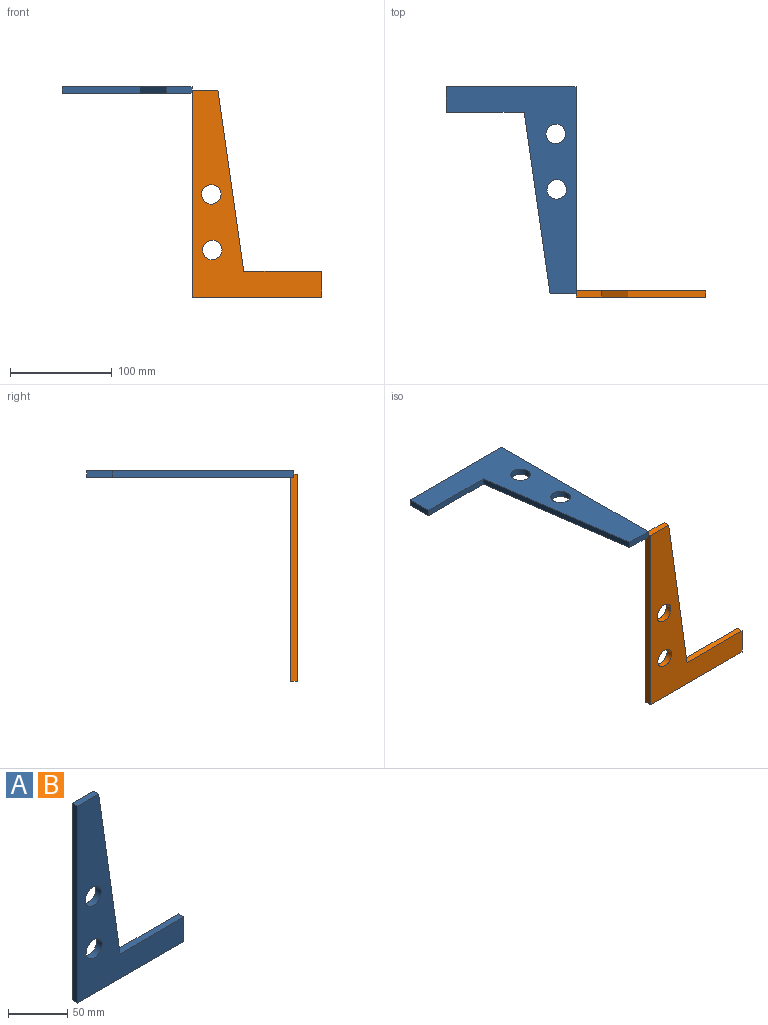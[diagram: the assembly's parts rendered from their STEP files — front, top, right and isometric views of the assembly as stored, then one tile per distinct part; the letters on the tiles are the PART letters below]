
ASSEMBLY  parts=2 mates=1
PART A: 10 faces, bbox 127x6.4x203.2 mm
  f0: plane 177.8x25.4mm, normal (0.99,0,0.14), area 1140.5mm2, adj f1,f5,f6,f7
  f1: plane 25.4x6.35mm, normal (0,0,1), area 161.3mm2, adj f0,f2,f6,f7
  f2: plane 203.2x6.35mm, normal (-1,0,0), area 1290.3mm2, adj f1,f3,f6,f7
  f3: plane 127x6.35mm, normal (0,0,-1), area 806.5mm2, adj f2,f4,f6,f7
  f4: plane 25.4x6.35mm, normal (1,0,0), area 161.3mm2, adj f3,f5,f6,f7
  f5: plane 76.2x6.35mm, normal (0,0,1), area 483.9mm2, adj f0,f4,f6,f7
  f6: plane 203.2x127mm, normal (0,-1,0), area 9429.9mm2, adj f0,f1,f2,f3,f4,f5,f8,f9
  f7: plane 203.2x127mm, normal (0,1,0), area 9429.9mm2, adj f0,f1,f2,f3,f4,f5,f8,f9
  f8: cylinder r=9.53mm len=19.05mm, axis (0,-1,0), area 380mm2, adj f6,f7
  f9: cylinder r=9.53mm len=19.05mm, axis (0,-1,0), area 380mm2, adj f6,f7
PART B: same geometry as A
PLACE A rot(axis=(0,-0.71,0.71),180deg) t=(0,180.98,203.2)mm
PLACE B t=(0,3.18,25.4)mm
MATE fastened A.f2 <-> B.f2  axis (1,0,0) through (0,3.17,203.2)mm
